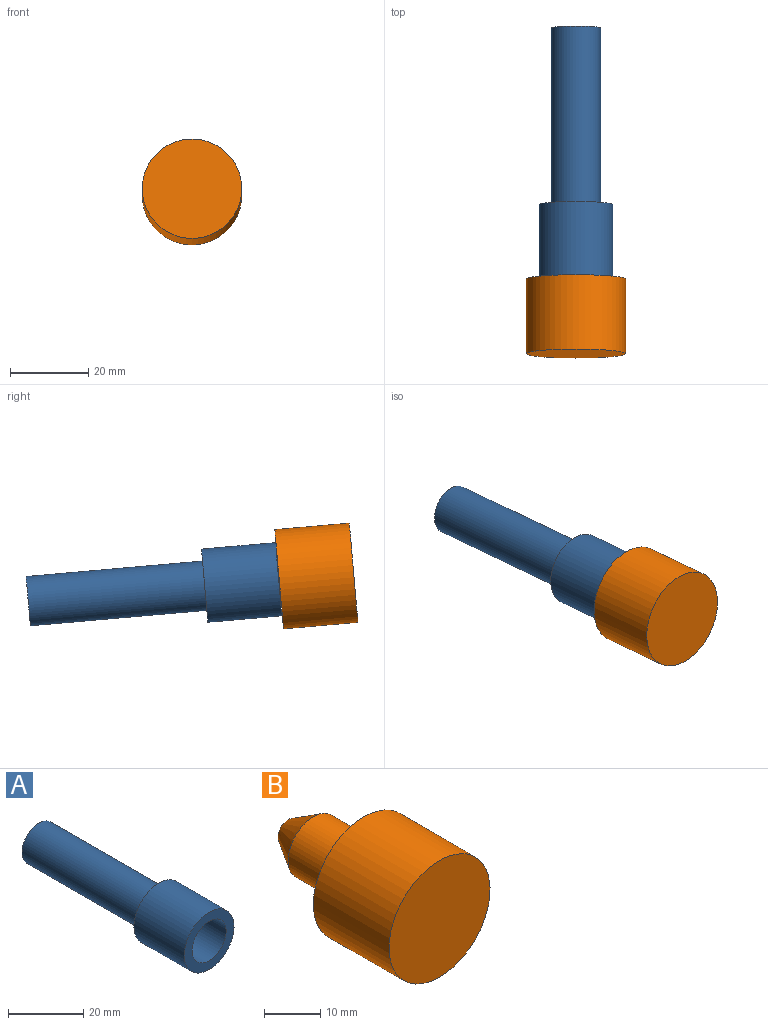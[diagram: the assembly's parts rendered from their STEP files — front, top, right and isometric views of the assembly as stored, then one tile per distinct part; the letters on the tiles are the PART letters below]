
ASSEMBLY  parts=2 mates=1
PART A: 8 faces, bbox 18.7x64.1x18.7 mm
  f0: cone r=2.54mm half-angle=31.7deg, axis (0,-1,0), area 207.3mm2, adj f1,f7
  f1: plane 5.08x5.08mm, normal (0,-1,0), area 20.3mm2, adj f0
  f2: plane 12.62x12.62mm, normal (0,1,0), area 125mm2, adj f3
  f3: cylinder r=6.31mm len=45.16mm, axis (0,1,0), area 1790mm2, adj f2,f4
  f4: plane 18.73x18.73mm, normal (0,1,0), area 150.5mm2, adj f3,f5
  f5: cylinder r=9.37mm len=18.92mm, axis (0,1,0), area 1113.3mm2, adj f4,f6
  f6: plane 18.73x18.73mm, normal (0,-1,0), area 146.5mm2, adj f5,f7
  f7: cylinder r=6.41mm len=12.82mm, axis (0,1,0), area 509.3mm2, adj f0,f6
PART B: 6 faces, bbox 25.4x38.1x25.4 mm
  f0: plane 5.08x5.08mm, normal (0,1,0), area 20.3mm2, adj f1
  f1: cone r=2.54mm half-angle=31deg, axis (0,-1,0), area 206.8mm2, adj f0,f2
  f2: cylinder r=6.35mm len=12.7mm, axis (0,-1,0), area 506.7mm2, adj f1,f3
  f3: plane 25.4x25.4mm, normal (0,1,0), area 380mm2, adj f2,f4
  f4: cylinder r=12.7mm len=25.4mm, axis (0,-1,0), area 1520.1mm2, adj f3,f5
  f5: plane 25.4x25.4mm, normal (0,-1,0), area 506.7mm2, adj f4
PLACE A rot(axis=(-1,0,0),5deg) t=(22.07,63.44,26.77)mm
PLACE B rot(axis=(-1,0,0),5deg) t=(22.07,63.44,26.77)mm
MATE fastened B.f1 <-> A.f0  axis (0,1,-0.09) through (22.07,63.44,26.77)mm
